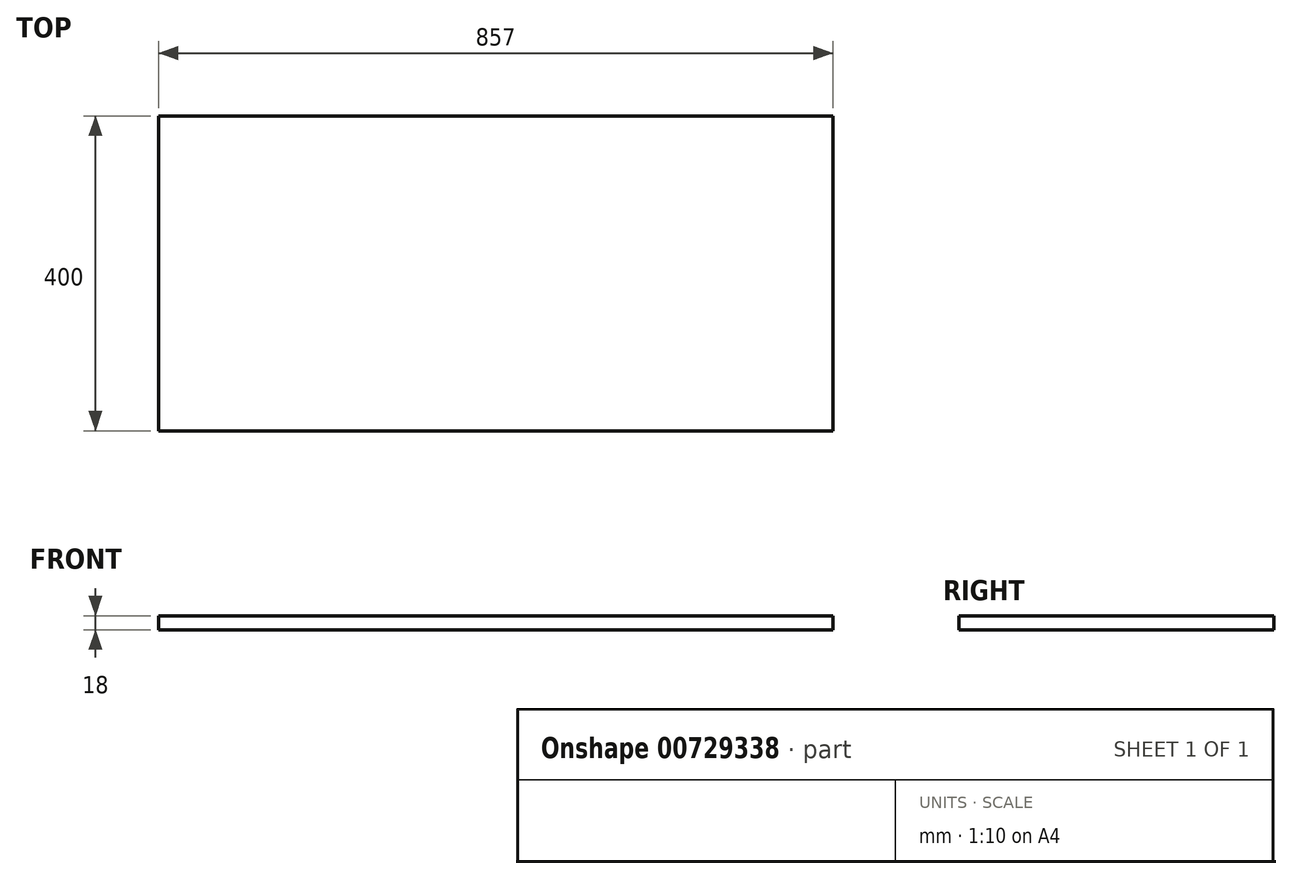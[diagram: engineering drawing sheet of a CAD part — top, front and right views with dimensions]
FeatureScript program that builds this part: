
annotation { "Feature Type Name" : "Feature", "Feature Type Description" : "" }
export const myFeature = defineFeature(function(context is Context, id is Id, definition is map)
    precondition{}
    {
        {
            var Q0;
            Q0=qCreatedBy(makeId("Front.planeOp"),FACE);
            var sketch = newSketch(context, id + "F0", { "sketchPlane" : qUnion([Q0])});
            skLineSegment(sketch, "E0.bottom", {"start": v(0, 0) * mm, "end": v(857, 0) * mm});
            skLineSegment(sketch, "E0.top", {"start": v(0, 18) * mm, "end": v(857, 18) * mm});
            skLineSegment(sketch, "E0.left", {"start": v(0, 0) * mm, "end": v(0, 18) * mm});
            skLineSegment(sketch, "E0.right", {"start": v(857, 0) * mm, "end": v(857, 18) * mm});
            skSolve(sketch);
        }
        {
            var Q0;
            Q0=makeQuery(id+"F0.imprint","IMPRINT",FACE,{"disambiguationData":[TD([[makeQuery(id+"F0.imprint","IMPRINT",EDGE,{"derivedFrom":sQuery(id+"F0.wireOp",EDGE,"E0.bottom")}),1.0]])]});
            extrude(context, id + "F1", {"entities" : qUnion([Q0]), "oppositeDirection" : true, "depth" : 400 * mm, "offsetDistance" : 25 * mm});
        }
    });
